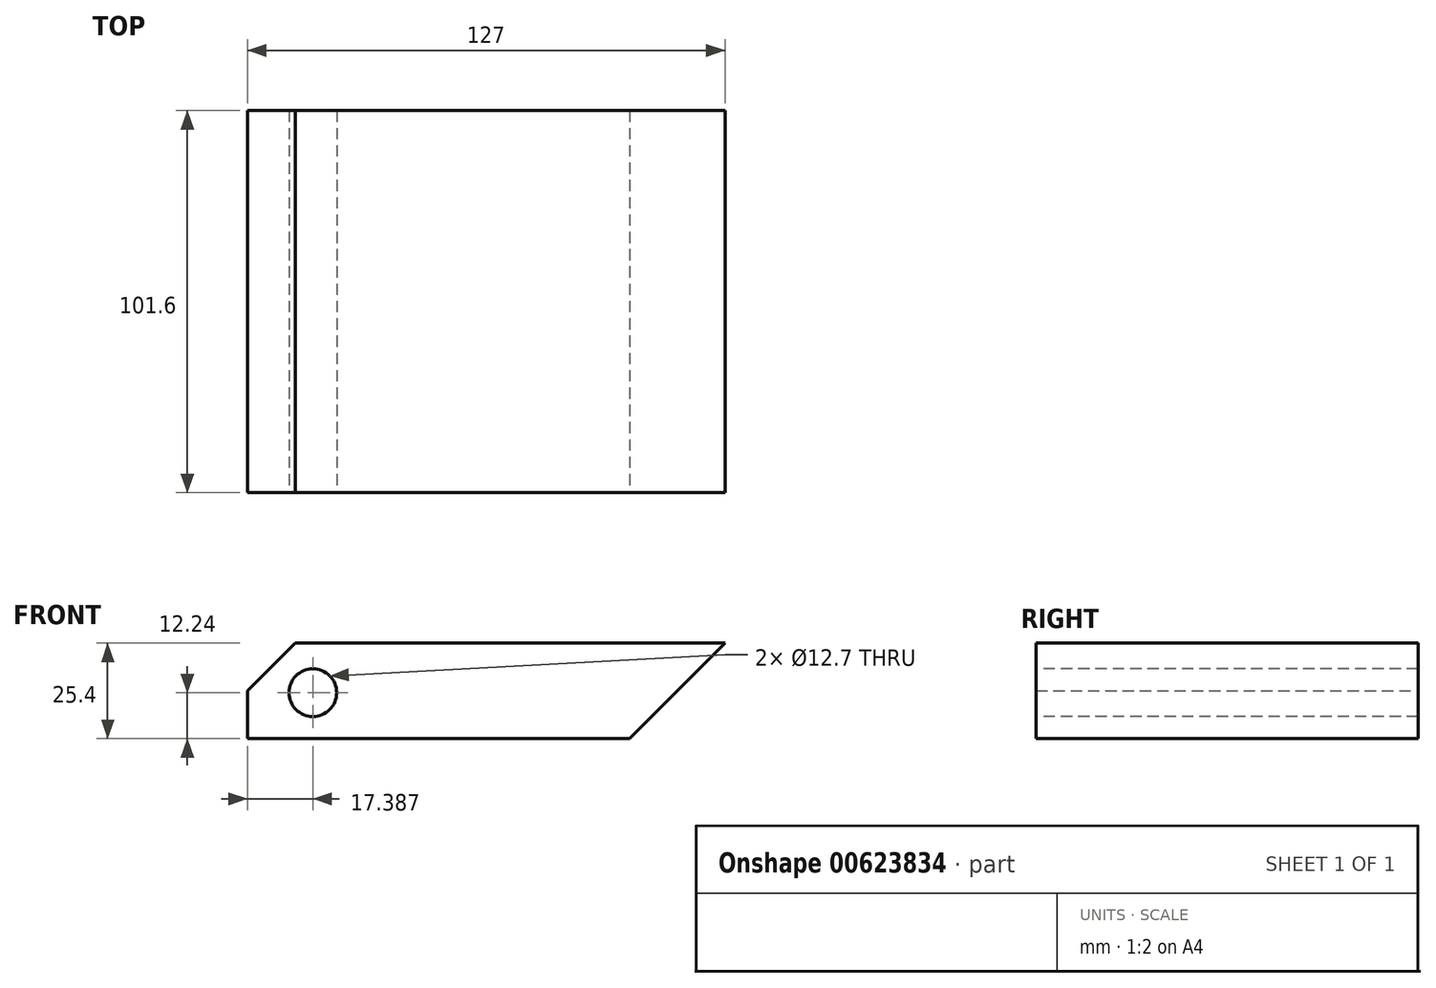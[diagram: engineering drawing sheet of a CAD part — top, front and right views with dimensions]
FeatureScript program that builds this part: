
annotation { "Feature Type Name" : "Feature", "Feature Type Description" : "" }
export const myFeature = defineFeature(function(context is Context, id is Id, definition is map)
    precondition{}
    {
        {
            var Q0;
            Q0=qCreatedBy(makeId("Front.planeOp"),FACE);
            var sketch = newSketch(context, id + "F0", { "sketchPlane" : qUnion([Q0])});
            skLineSegment(sketch, "E0.bottom", {"start": v(-57.85, 13.16) * mm, "end": v(69.15, 13.16) * mm});
            skLineSegment(sketch, "E0.top", {"start": v(-57.85, -12.24) * mm, "end": v(69.15, -12.24) * mm});
            skLineSegment(sketch, "E0.left", {"start": v(-57.85, 13.16) * mm, "end": v(-57.85, -12.24) * mm});
            skLineSegment(sketch, "E0.right", {"start": v(69.15, 13.16) * mm, "end": v(69.15, -12.24) * mm});
            skCircle(sketch, "E1", {"center": v(-40.46, 0) * mm, "radius": 6.35 * mm});
            skSolve(sketch);
        }
        {
            var Q0;
            Q0=makeQuery(id+"F0.imprint","IMPRINT",FACE,{"disambiguationData":[TD([[makeQuery(id+"F0.imprint","IMPRINT",EDGE,{"derivedFrom":sQuery(id+"F0.wireOp",EDGE,"E0.bottom")}),-1.0]])]});
            extrude(context, id + "F1", {"entities" : qUnion([Q0]), "oppositeDirection" : true, "depth" : 101.6 * mm, "offsetDistance" : 25.4 * mm});
        }
        {
            var Q0;
            Q0=makeQuery(id+"F1.opExtrude","SWEPT_EDGE",EDGE,{"disambiguationData":[OSD([sQuery(id+"F0.wireOp",EDGE,"E0.top"),sQuery(id+"F0.wireOp",EDGE,"E0.right")])]});
            chamfer(context, id + "F2", {"entities" : qUnion([Q0]), "width" : 25.4 * mm, "tangentPropagation" : true});
        }
        {
            var Q0;
            Q0=makeQuery(id+"F1.opExtrude","SWEPT_EDGE",EDGE,{"disambiguationData":[OSD([sQuery(id+"F0.wireOp",EDGE,"E0.bottom"),sQuery(id+"F0.wireOp",EDGE,"E0.left")])]});
            chamfer(context, id + "F3", {"entities" : qUnion([Q0]), "width" : 12.7 * mm, "tangentPropagation" : true});
        }
    });
